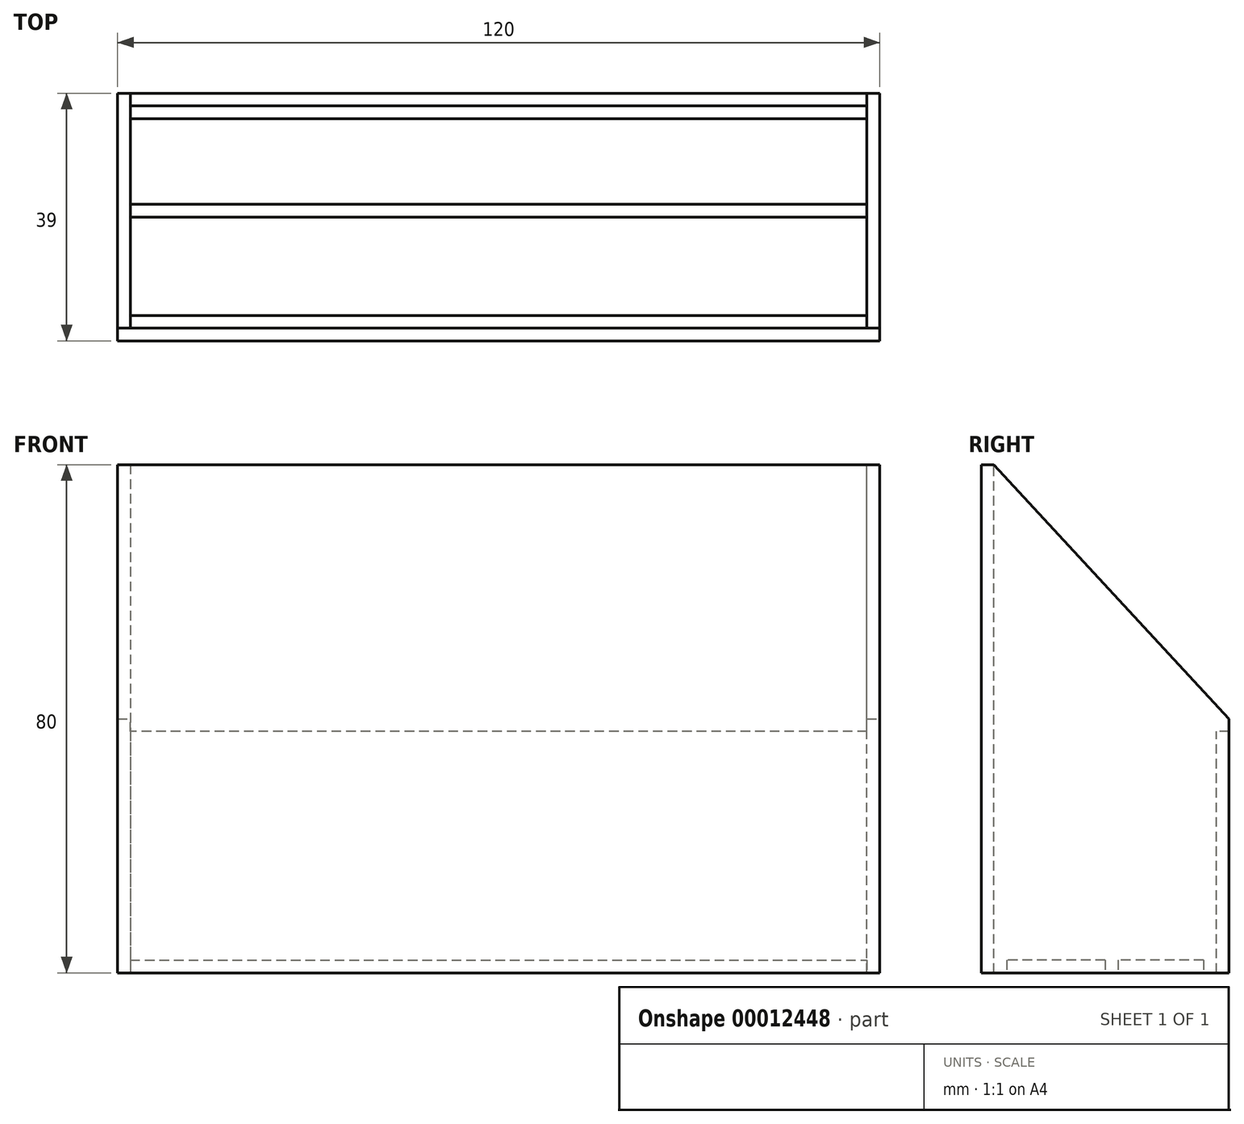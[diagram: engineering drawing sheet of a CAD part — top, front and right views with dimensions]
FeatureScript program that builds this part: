
annotation { "Feature Type Name" : "Feature", "Feature Type Description" : "" }
export const myFeature = defineFeature(function(context is Context, id is Id, definition is map)
    precondition{}
    {
        {
            var Q0;
            Q0=qCreatedBy(makeId("Front.planeOp"),FACE);
            var sketch = newSketch(context, id + "F0", { "sketchPlane" : qUnion([Q0])});
            skLineSegment(sketch, "E0.bottom", {"start": v(0, 0) * mm, "end": v(-120, 0) * mm});
            skLineSegment(sketch, "E0.top", {"start": v(0, 38) * mm, "end": v(-120, 38) * mm});
            skLineSegment(sketch, "E0.left", {"start": v(0, 0) * mm, "end": v(0, 38) * mm});
            skLineSegment(sketch, "E0.right", {"start": v(-120, 0) * mm, "end": v(-120, 38) * mm});
            skSolve(sketch);
        }
        {
            var Q0;
            Q0 = qSketchRegion(id + "F0", true);
            extrude(context, id + "F1", {"entities" : qUnion([Q0]), "depth" : 2 * mm});
        }
        {
            var Q0;
            Q0=qCreatedBy(makeId("Right.planeOp"),FACE);
            var sketch = newSketch(context, id + "F2", { "sketchPlane" : qUnion([Q0])});
            skLineSegment(sketch, "E1.bottom", {"start": v(0, 0) * mm, "end": v(-37, 0) * mm});
            skLineSegment(sketch, "E1.top", {"start": v(0, 80) * mm, "end": v(-37, 80) * mm});
            skLineSegment(sketch, "E1.left", {"start": v(0, 0) * mm, "end": v(0, 80) * mm});
            skLineSegment(sketch, "E1.right", {"start": v(-37, 0) * mm, "end": v(-37, 80) * mm});
            skSolve(sketch);
        }
        {
            var Q0;
            Q0 = qSketchRegion(id + "F2", true);
            extrude(context, id + "F3", {"entities" : qUnion([Q0]), "operationType" : NewBodyOperationType.ADD, "oppositeDirection" : true, "depth" : 2 * mm});
        }
        {
            var Q0;
            Q0=makeQuery(id+"F3.opExtrude","SWEPT_FACE",FACE,{"disambiguationData":[OSD([sQuery(id+"F2.wireOp",EDGE,"E1.right")])]});
            var sketch = newSketch(context, id + "F4", { "sketchPlane" : qUnion([Q0])});
            skLineSegment(sketch, "E2.bottom", {"start": v(0, 0) * mm, "end": v(-120, 0) * mm});
            skLineSegment(sketch, "E2.top", {"start": v(0, 80) * mm, "end": v(-120, 80) * mm});
            skLineSegment(sketch, "E2.left", {"start": v(0, 0) * mm, "end": v(0, 80) * mm});
            skLineSegment(sketch, "E2.right", {"start": v(-120, 0) * mm, "end": v(-120, 80) * mm});
            skSolve(sketch);
        }
        {
            var Q0;
            Q0 = qSketchRegion(id + "F4", true);
            extrude(context, id + "F5", {"entities" : qUnion([Q0]), "operationType" : NewBodyOperationType.ADD, "depth" : 2 * mm});
        }
        {
            var Q0;
            Q0=makeQuery(id+"F5.opExtrude","SWEPT_FACE",FACE,{"disambiguationData":[OSD([sQuery(id+"F4.wireOp",EDGE,"E2.right")])]});
            var sketch = newSketch(context, id + "F6", { "sketchPlane" : qUnion([Q0])});
            skLineSegment(sketch, "E3.bottom", {"start": v(39, 0) * mm, "end": v(0, 0) * mm});
            skLineSegment(sketch, "E3.top", {"start": v(39, 80) * mm, "end": v(0, 80) * mm});
            skLineSegment(sketch, "E3.left", {"start": v(39, 0) * mm, "end": v(39, 80) * mm});
            skLineSegment(sketch, "E3.right", {"start": v(0, 0) * mm, "end": v(0, 80) * mm});
            skSolve(sketch);
        }
        {
            var Q0;
            Q0 = qSketchRegion(id + "F6", true);
            extrude(context, id + "F7", {"entities" : qUnion([Q0]), "operationType" : NewBodyOperationType.ADD, "oppositeDirection" : true, "depth" : 2 * mm});
        }
        {
            var Q0;
            {var subQ0=sQuery(id+"F6.wireOp",EDGE,"E3.bottom");Q0=makeQuery(id+"FPmHALdMYyZreVW_1.boolean.opBoolean","MERGE",FACE,{"derivedFrom":[makeQuery(id+"F7.boolean.opBoolean","MERGE",FACE,{"derivedFrom":[makeQuery(id+"F5.boolean.opBoolean","MERGE",FACE,{"derivedFrom":[makeQuery(id+"F3.boolean.opBoolean","MERGE",FACE,{"derivedFrom":[makeQuery(id+"F1.opExtrude","SWEPT_FACE",FACE,{"disambiguationData":[OSD([sQuery(id+"F0.wireOp",EDGE,"E0.bottom")])]}),makeQuery(id+"F3.opExtrude","SWEPT_FACE",FACE,{"disambiguationData":[OSD([sQuery(id+"F2.wireOp",EDGE,"E1.bottom")])]})]}),makeQuery(id+"F5.opExtrude","SWEPT_FACE",FACE,{"disambiguationData":[OSD([sQuery(id+"F4.wireOp",EDGE,"E2.bottom")])]})]}),makeQuery(id+"F7.opExtrude","SWEPT_FACE",FACE,{"disambiguationData":[OSD([subQ0])]})]}),makeQuery(id+"FPmHALdMYyZreVW_1.opExtrude","SWEPT_FACE",FACE,{"disambiguationData":[OSD([subQ0])]})]});}
            var sketch = newSketch(context, id + "F8", { "sketchPlane" : qUnion([Q0])});
            skLineSegment(sketch, "E4.bottom", {"start": v(-118, 4) * mm, "end": v(-2, 4) * mm});
            skLineSegment(sketch, "E4.top", {"start": v(-118, 17.5) * mm, "end": v(-2, 17.5) * mm});
            skLineSegment(sketch, "E4.left", {"start": v(-118, 4) * mm, "end": v(-118, 17.5) * mm});
            skLineSegment(sketch, "E4.right", {"start": v(-2, 4) * mm, "end": v(-2, 17.5) * mm});
            skLineSegment(sketch, "E5.bottom", {"start": v(-2, 19.5) * mm, "end": v(-118, 19.5) * mm});
            skLineSegment(sketch, "E5.top", {"start": v(-2, 35) * mm, "end": v(-118, 35) * mm});
            skLineSegment(sketch, "E5.left", {"start": v(-2, 19.5) * mm, "end": v(-2, 35) * mm});
            skLineSegment(sketch, "E5.right", {"start": v(-118, 19.5) * mm, "end": v(-118, 35) * mm});
            skSolve(sketch);
        }
        {
            var Q0;
            Q0 = qSketchRegion(id + "F8", true);
            extrude(context, id + "F9", {"entities" : qUnion([Q0]), "operationType" : NewBodyOperationType.ADD, "oppositeDirection" : true, "depth" : 2 * mm});
        }
        {
            var Q0;
            Q0=makeQuery(id+"F5.boolean.opBoolean","MERGE",FACE,{"derivedFrom":[makeQuery(id+"F3.boolean.opBoolean","MERGE",FACE,{"derivedFrom":[makeQuery(id+"F1.opExtrude","SWEPT_FACE",FACE,{"disambiguationData":[OSD([sQuery(id+"F0.wireOp",EDGE,"E0.left")])]}),makeQuery(id+"F3.opExtrude","CAP_FACE",FACE,{"disambiguationData":[OSD([sQuery(id+"F2.wireOp",EDGE,"E1.bottom"),sQuery(id+"F2.wireOp",EDGE,"E1.top"),sQuery(id+"F2.wireOp",EDGE,"E1.left"),sQuery(id+"F2.wireOp",EDGE,"E1.right")])],"isStart":true})]}),makeQuery(id+"F5.opExtrude","SWEPT_FACE",FACE,{"disambiguationData":[OSD([sQuery(id+"F4.wireOp",EDGE,"E2.left")])]})]});
            var sketch = newSketch(context, id + "F10", { "sketchPlane" : qUnion([Q0])});
            skLineSegment(sketch, "E6.bottom", {"start": v(0, 80) * mm, "end": v(-37, 80) * mm});
            skLineSegment(sketch, "E6.left", {"start": v(0, 80) * mm, "end": v(0, 40) * mm});
            skLineSegment(sketch, "E7", {"start": v(0, 40) * mm, "end": v(-37, 80) * mm});
            skSolve(sketch);
        }
        {
            var Q0;
            Q0 = qSketchRegion(id + "F10", true);
            extrude(context, id + "F11", {"entities" : qUnion([Q0]), "operationType" : NewBodyOperationType.REMOVE, "oppositeDirection" : true, "depth" : 120 * mm});
        }
    });
